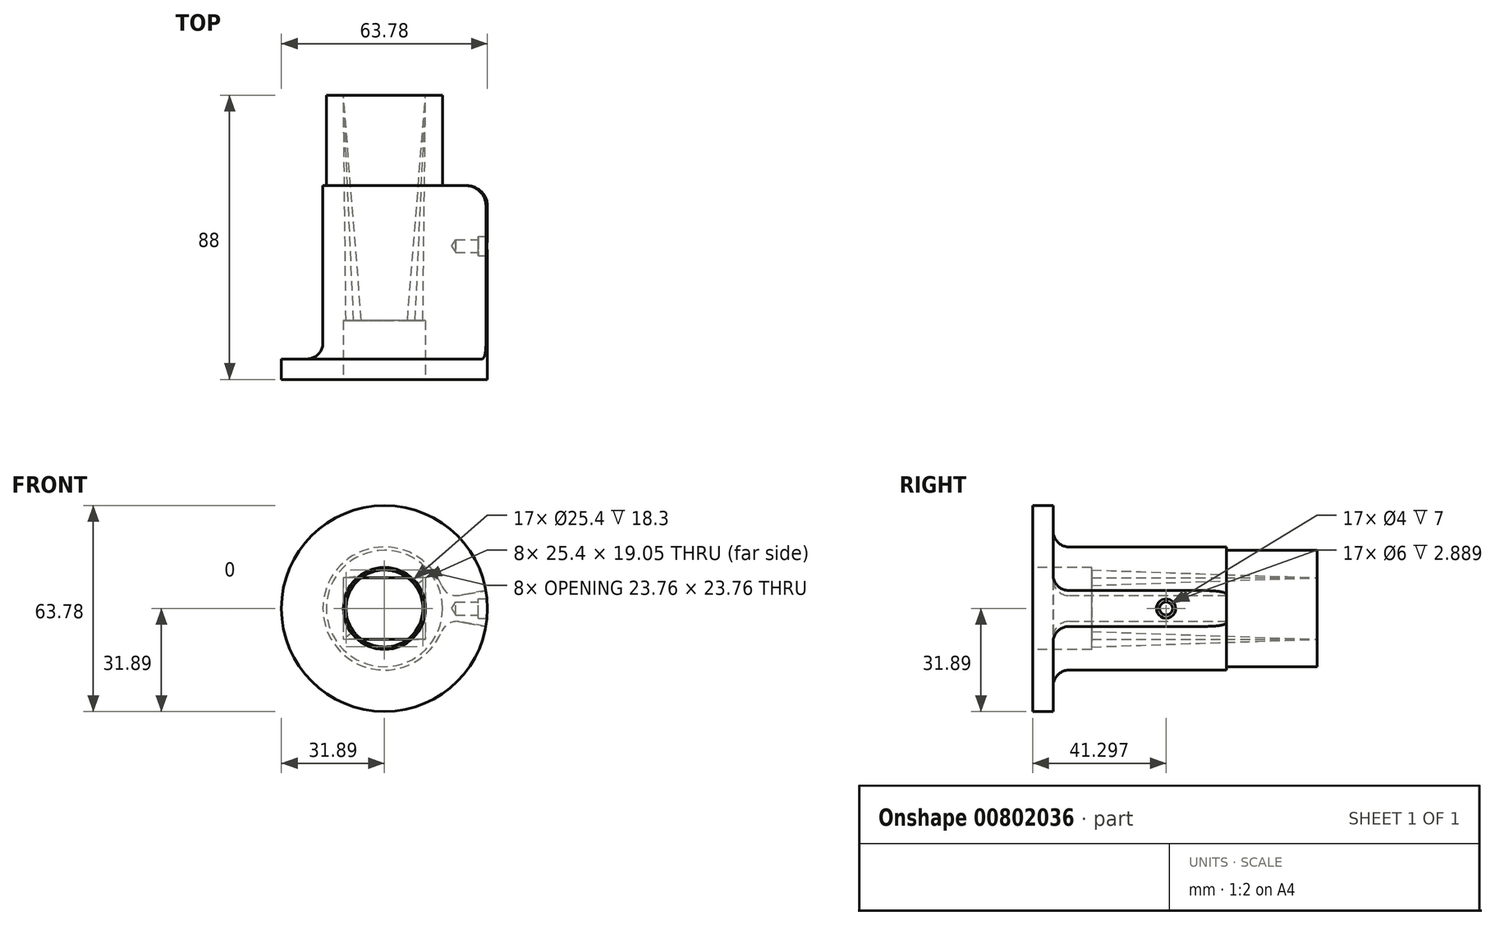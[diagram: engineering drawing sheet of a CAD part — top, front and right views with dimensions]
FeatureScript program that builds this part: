
annotation { "Feature Type Name" : "Feature", "Feature Type Description" : "" }
export const myFeature = defineFeature(function(context is Context, id is Id, definition is map)
    precondition{}
    {
        {
            var Q0;
            Q0=qCreatedBy(makeId("Right.planeOp"),FACE);
            var sketch = newSketch(context, id + "F0", { "sketchPlane" : qUnion([Q0])});
            skLineSegment(sketch, "E0", {"start": v(-91.81, 0) * mm, "end": v(-91.81, 31.89) * mm});
            skLineSegment(sketch, "E1", {"start": v(-91.81, 31.89) * mm, "end": v(-38.16, 31.89) * mm});
            skLineSegment(sketch, "E2", {"start": v(-91.81, 0) * mm, "end": v(-3.81, 0) * mm});
            skLineSegment(sketch, "E3", {"start": v(-3.81, 0) * mm, "end": v(-3.81, 18) * mm});
            skLineSegment(sketch, "E4", {"start": v(-3.81, 18) * mm, "end": v(-31.81, 18) * mm});
            skLineSegment(sketch, "E5", {"start": v(-31.81, 18) * mm, "end": v(-31.81, 25.54) * mm});
            skPoint(sketch, "E6.visualSharp", {"position": v(-31.81, 31.89) * mm});
            skArc(sketch, "E6.filletArc", {"start": v(-31.81, 25.54) * mm, "mid": v(-33.67, 30.03) * mm, "end": v(-38.16, 31.89) * mm});
            skSolve(sketch);
        }
        {
            var Q0;
            Q0=qSketchRegion(id+"F0",true);
            var Q1;
            Q1=sQuery(id+"F0.wireOp",EDGE,"E2");
            revolve(context, id + "F1", {"entities" : qUnion([Q0]), "axis" : qUnion([Q1]), "revolveType" : RevolveType.FULL});
        }
        {
            var Q0;
            Q0=makeQuery(id+"F1.opRevolve","SWEPT_FACE",FACE,{"disambiguationData":[OSD([sQuery(id+"F0.wireOp",EDGE,"E3")])]});
            var sketch = newSketch(context, id + "F2", { "sketchPlane" : qUnion([Q0])});
            skLineSegment(sketch, "E7.bottom", {"start": v(-12.7, 9.52) * mm, "end": v(12.7, 9.52) * mm});
            skLineSegment(sketch, "E7.top", {"start": v(-12.7, -9.53) * mm, "end": v(12.7, -9.53) * mm});
            skLineSegment(sketch, "E7.left", {"start": v(-12.7, 9.52) * mm, "end": v(-12.7, -9.52) * mm});
            skLineSegment(sketch, "E7.right", {"start": v(12.7, 9.52) * mm, "end": v(12.7, -9.53) * mm});
            skSolve(sketch);
        }
        {
            var Q0;
            Q0=makeQuery(id+"F1.opRevolve","SWEPT_FACE",FACE,{"disambiguationData":[OSD([sQuery(id+"F0.wireOp",EDGE,"E0")])]});
            var sketch = newSketch(context, id + "F3", { "sketchPlane" : qUnion([Q0])});
            skCircle(sketch, "E8", {"center": v(0, 0) * mm, "radius": 12.7 * mm});
            skSolve(sketch);
        }
        {
            var Q0;
            Q0=qSketchRegion(id+"F3",true);
            extrude(context, id + "F4", {"entities" : qUnion([Q0]), "operationType" : NewBodyOperationType.REMOVE, "oppositeDirection" : true, "depth" : 18.3 * mm});
        }
        {
            var Q0;
            Q0=makeQuery(id+"F4.boolean.opBoolean","COPY",FACE,{"derivedFrom":makeQuery(id+"F4.opExtrude","CAP_FACE",FACE,{"disambiguationData":[OSD([sQuery(id+"F3.wireOp",EDGE,"E8")])],"isStart":false})});
            var sketch = newSketch(context, id + "F5", { "sketchPlane" : qUnion([Q0])});
            skCircle(sketch, "E9", {"center": v(0, 0) * mm, "radius": 11.9 * mm});
            skSolve(sketch);
        }
        {
            var Q1;
            Q1=qSketchRegion(id+"F5",true);
            var Q2;
            Q2=qSketchRegion(id+"F2",true);
            loft(context, id + "F6", {"operationType" : NewBodyOperationType.REMOVE, "sheetProfilesArray" : [{ "sheetProfileEntities" : qUnion([Q1]) }, { "sheetProfileEntities" : qUnion([Q2]) }]});
        }
        {
            var Q0;
            Q0=qCreatedBy(makeId("Right.planeOp"),FACE);
            cPlane(context, id + "F7", {"entities" : qUnion([Q0]), "cplaneType" : CPlaneType.OFFSET, "offset" : 32 * mm, "width" : 150 * mm, "height" : 150 * mm});
        }
        {
            var Q0;
            Q0=qCreatedBy(id+"F7.planeOp",FACE);
            var sketch = newSketch(context, id + "F8", { "sketchPlane" : qUnion([Q0])});
            skLineSegment(sketch, "E10", {"start": v(0, 0) * mm, "end": v(-115.51, 0) * mm, "construction": true});
            skPoint(sketch, "E11", {"position": v(-50.51, 0) * mm});
            skSolve(sketch);
        }
        {
            var Q0;
            Q0=sQuery(id+"F8.wireOp",VERTEX,"E11");
            var Q1;
            Q1=makeQuery(id+"F1.opRevolve","SWEPT_BODY",BODY,{"disambiguationData":[OSD([sQuery(id+"F0.wireOp",EDGE,"E0"),sQuery(id+"F0.wireOp",EDGE,"E1"),sQuery(id+"F0.wireOp",EDGE,"E2"),sQuery(id+"F0.wireOp",EDGE,"E3"),sQuery(id+"F0.wireOp",EDGE,"E4"),sQuery(id+"F0.wireOp",EDGE,"E5"),sQuery(id+"F0.wireOp",EDGE,"E6.filletArc")])]});
            hole(context, id + "F9", {"style" : HoleStyle.C_BORE, "endStyle" : HoleEndStyle.BLIND, "holeDiameter" : 4 * mm, "cBoreDiameter" : 6 * mm, "cBoreDepth" : 3 * mm, "holeDepth" : 10 * mm, "isTappedThrough" : true, "tappedDepth" : 46.25 * mm, "tapClearance" : 3, "startFromSketch" : true, "locations" : qUnion([Q0]), "scope" : qUnion([Q1])});
        }
        {
            var Q0;
            Q0=qCreatedBy(makeId("Right.planeOp"),FACE);
            var sketch = newSketch(context, id + "F10", { "sketchPlane" : qUnion([Q0])});
            skLineSegment(sketch, "E12.bottom", {"start": v(-85.46, 47.2) * mm, "end": v(-25.54, 47.2) * mm});
            skLineSegment(sketch, "E12.top", {"start": v(-80.46, 19.05) * mm, "end": v(-30.54, 19.05) * mm});
            skLineSegment(sketch, "E12.left", {"start": v(-85.46, 47.2) * mm, "end": v(-85.46, 24.05) * mm});
            skLineSegment(sketch, "E12.right", {"start": v(-25.54, 47.2) * mm, "end": v(-25.54, 24.05) * mm});
            skPoint(sketch, "E13.visualSharp", {"position": v(-85.46, 19.05) * mm});
            skArc(sketch, "E13.filletArc", {"start": v(-85.46, 24.05) * mm, "mid": v(-84, 20.51) * mm, "end": v(-80.46, 19.05) * mm});
            skPoint(sketch, "E14.visualSharp", {"position": v(-25.54, 19.05) * mm});
            skArc(sketch, "E14.filletArc", {"start": v(-30.54, 19.05) * mm, "mid": v(-27, 20.51) * mm, "end": v(-25.54, 24.05) * mm});
            skSolve(sketch);
        }
        {
            var Q0;
            Q0=qSketchRegion(id+"F10",true);
            var Q1;
            Q1=makeQuery(id+"F1.opRevolve","SWEPT_EDGE",EDGE,{"disambiguationData":[OSD([sQuery(id+"F0.wireOp",EDGE,"E0"),sQuery(id+"F0.wireOp",EDGE,"E1")])]});
            revolve(context, id + "F11", {"operationType" : NewBodyOperationType.REMOVE, "surfaceOperationType" : NewSurfaceOperationType.NEW, "entities" : qUnion([Q0]), "axis" : qUnion([Q1]), "revolveType" : RevolveType.TWO_DIRECTIONS, "angle" : 260 * degree, "angleBack" : 280 * degree});
        }
        {
            var Q0;
            Q0=qCreatedBy(makeId("Right.planeOp"),FACE);
            var sketch = newSketch(context, id + "F12", { "sketchPlane" : qUnion([Q0])});
            skLineSegment(sketch, "E15.bottom", {"start": v(-85.46, 47.2) * mm, "end": v(-55.46, 47.2) * mm});
            skLineSegment(sketch, "E15.top", {"start": v(-80.46, 19.05) * mm, "end": v(-60.46, 19.05) * mm});
            skLineSegment(sketch, "E15.left", {"start": v(-85.46, 47.2) * mm, "end": v(-85.46, 24.05) * mm});
            skLineSegment(sketch, "E15.right", {"start": v(-55.46, 47.2) * mm, "end": v(-55.46, 24.05) * mm});
            skPoint(sketch, "E16.visualSharp", {"position": v(-85.46, 19.05) * mm});
            skArc(sketch, "E16.filletArc", {"start": v(-85.46, 24.05) * mm, "mid": v(-84, 20.51) * mm, "end": v(-80.46, 19.05) * mm});
            skPoint(sketch, "E17.visualSharp", {"position": v(-55.46, 19.05) * mm});
            skArc(sketch, "E17.filletArc", {"start": v(-60.46, 19.05) * mm, "mid": v(-56.93, 20.51) * mm, "end": v(-55.46, 24.05) * mm});
            skSolve(sketch);
        }
        {
            var Q0;
            Q0=makeQuery(id+"F11.boolean.opBoolean","COPY",EDGE,{"derivedFrom":makeQuery(id+"F11.opRevolve","CAP_EDGE",EDGE,{"disambiguationData":[OSD([sQuery(id+"F10.wireOp",EDGE,"E12.top")])],"isStart":true})});
            var Q1;
            Q1=makeQuery(id+"F11.boolean.opBoolean","COPY",EDGE,{"derivedFrom":makeQuery(id+"F11.opRevolve","CAP_EDGE",EDGE,{"disambiguationData":[OSD([sQuery(id+"F10.wireOp",EDGE,"E12.top")])],"isStart":false})});
            fillet(context, id + "F13", {"entities" : qUnion([Q0, Q1]), "tangentPropagation" : true, "radius" : 5 * mm, "defaultsChanged" : false, "vertexSettings" : [], "allowEdgeOverflow" : false});
        }
    });
